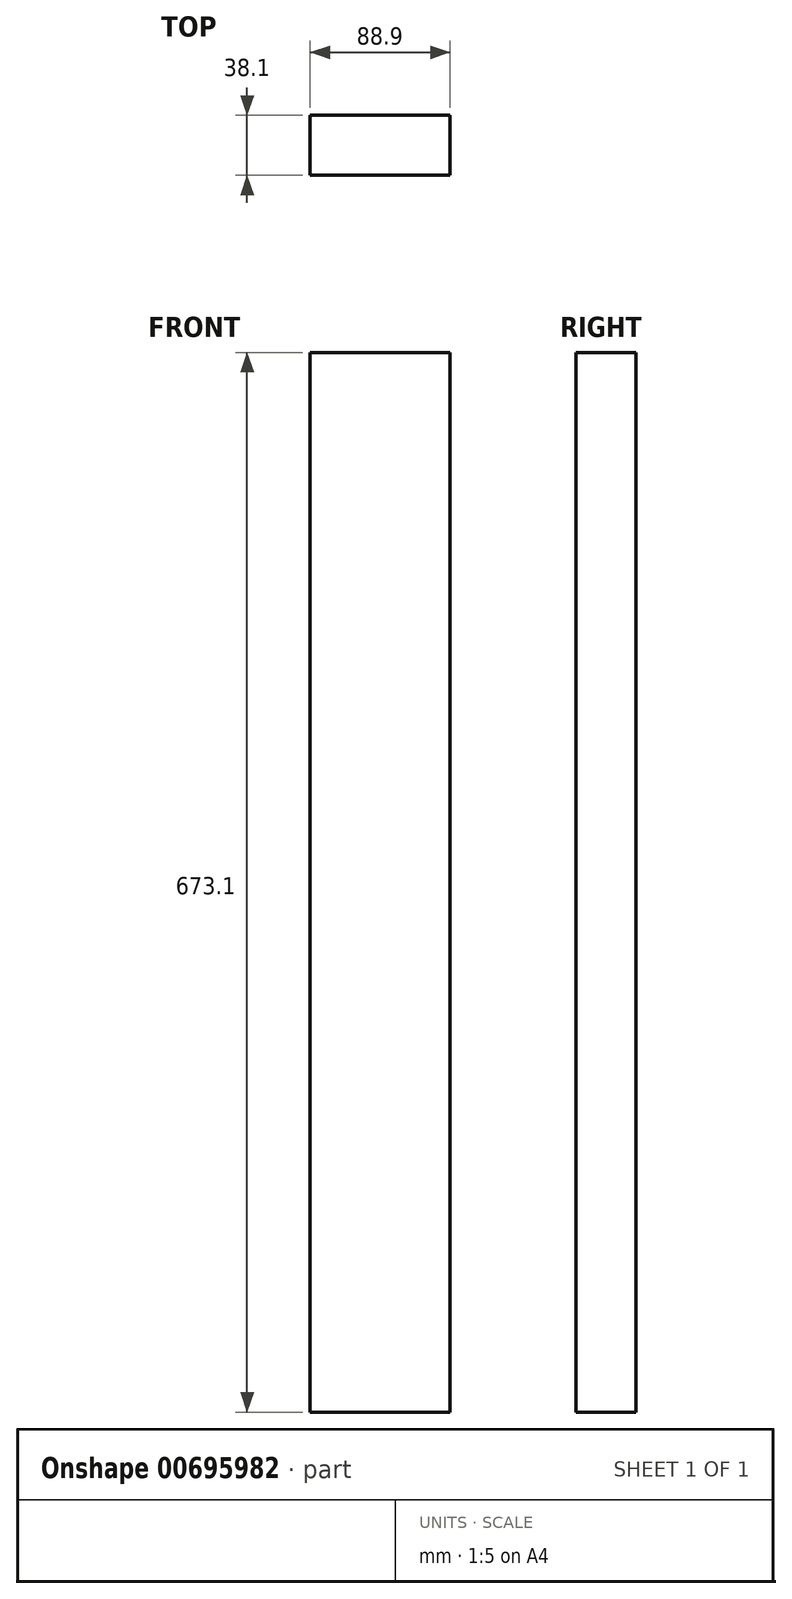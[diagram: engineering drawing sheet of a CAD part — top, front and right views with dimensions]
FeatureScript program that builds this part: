
annotation { "Feature Type Name" : "Feature", "Feature Type Description" : "" }
export const myFeature = defineFeature(function(context is Context, id is Id, definition is map)
    precondition{}
    {
        {
            var Q0;
            Q0=qCreatedBy(makeId("Front.planeOp"),FACE);
            var sketch = newSketch(context, id + "F0", { "sketchPlane" : qUnion([Q0])});
            skLineSegment(sketch, "E0.bottom", {"start": v(0, 0) * mm, "end": v(88.9, 0) * mm});
            skLineSegment(sketch, "E0.top", {"start": v(0, 673.1) * mm, "end": v(88.9, 673.1) * mm});
            skLineSegment(sketch, "E0.left", {"start": v(0, 0) * mm, "end": v(0, 673.1) * mm});
            skLineSegment(sketch, "E0.right", {"start": v(88.9, 0) * mm, "end": v(88.9, 673.1) * mm});
            skSolve(sketch);
        }
        {
            var Q0;
            Q0=makeQuery(id+"F0.imprint","IMPRINT",FACE,{"disambiguationData":[TD([[makeQuery(id+"F0.imprint","IMPRINT",EDGE,{"derivedFrom":sQuery(id+"F0.wireOp",EDGE,"E0.bottom")}),1.0]])]});
            extrude(context, id + "F1", {"entities" : qUnion([Q0]), "depth" : 38.1 * mm, "offsetDistance" : 25.4 * mm});
        }
    });
